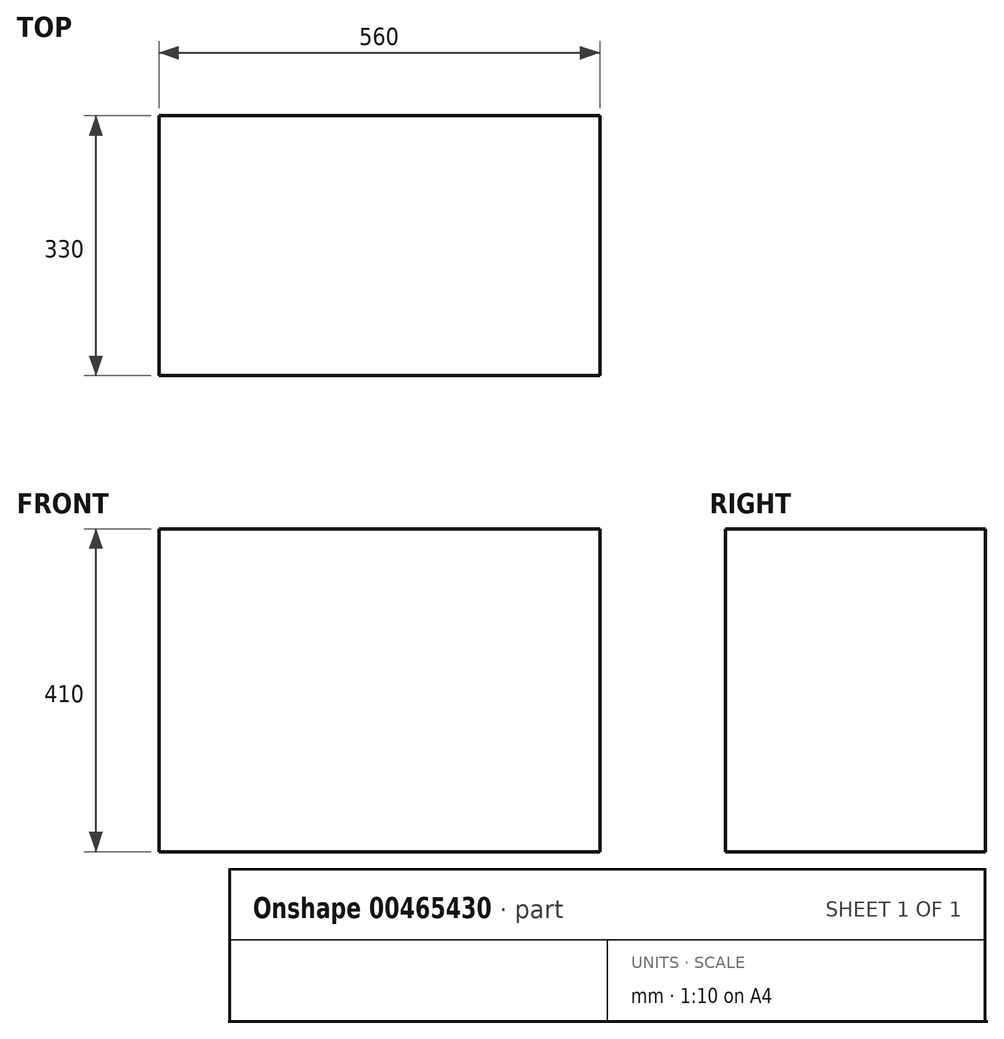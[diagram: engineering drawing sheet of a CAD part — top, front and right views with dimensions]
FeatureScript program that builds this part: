
annotation { "Feature Type Name" : "Feature", "Feature Type Description" : "" }
export const myFeature = defineFeature(function(context is Context, id is Id, definition is map)
    precondition{}
    {
        {
            var Q0;
            Q0=qCreatedBy(makeId("Top.planeOp"),FACE);
            var sketch = newSketch(context, id + "F0", { "sketchPlane" : qUnion([Q0])});
            skLineSegment(sketch, "E0.bottom", {"start": v(0, 0) * mm, "end": v(560, 0) * mm});
            skLineSegment(sketch, "E0.top", {"start": v(0, 330) * mm, "end": v(560, 330) * mm});
            skLineSegment(sketch, "E0.left", {"start": v(0, 0) * mm, "end": v(0, 330) * mm});
            skLineSegment(sketch, "E0.right", {"start": v(560, 0) * mm, "end": v(560, 330) * mm});
            skSolve(sketch);
        }
        {
            var Q0;
            Q0=makeQuery(id+"F0.imprint","IMPRINT",FACE,{"disambiguationData":[TD([[makeQuery(id+"F0.imprint","IMPRINT",EDGE,{"derivedFrom":sQuery(id+"F0.wireOp",EDGE,"E0.bottom")}),1.0]])]});
            extrude(context, id + "F1", {"entities" : qUnion([Q0]), "depth" : 410 * mm});
        }
    });
